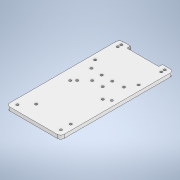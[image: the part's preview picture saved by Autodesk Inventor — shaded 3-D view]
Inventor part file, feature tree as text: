
AUTODESK INVENTOR PART (.ipt)
format: ipt  version: 2022.6 (Build 266554000, 554)  size: 208,384 bytes
history: native  units: mm
features: hole x5, sketch x5, projected_geometry x2, extrude x1, fillet x1, other x1
ambient origin geometry x8: Origin, YZ Plane, XZ Plane, XY Plane, X Axis, Y Axis, Z Axis, Center Point
bodies: Solid1 (feature_tree)
feature tree (15):
  extrude  "Extrusion1"  Depth=160.0mm
  fillet  "Fillet1"  Radius=5.0mm
  hole  "Brass stands"  [1 undecoded]
  hole  "Battery mount"  [1 undecoded]
  hole  "pi cam"  [1 undecoded]
  hole  "raspberry pi"  [1 undecoded]
  hole  "Hole7"  [1 undecoded]
  sketch  "Sketch1"  dims[d0=77.0mm d1=160.0mm d2=5.0mm d3=0.0mm]
  sketch  "Sketch3"  dims[d4=5.0mm]
  sketch  "Sketch5"  dims[d8=3.4mm d9=6.0mm d10=4.0mm d11=2.0mm d12=90.0deg d13=8.0mm d14=20.594885mm d15=147.0mm]
  sketch  "Sketch7"  dims[d18=8.0mm d31=30.0mm]
  sketch  "Sketch8"  dims[d32=46.0mm d33=55.0mm d34=3.4mm d35=6.0mm d36=4.0mm d37=2.0mm d38=90.0deg d39=8.0mm d40=20.594885mm d56=61.5mm d64=45.0mm d65=5.0mm d66=13.5mm d67=15.0mm d71=51.0mm d72=3.4mm d73=6.0mm d74=4.0mm d75=2.0mm d76=90.0deg d77=8.0mm d78=20.594885mm d79=49.0mm d80=58.0mm d81=22.0mm d82=7.75mm d83=3.4mm d84=6.0mm d85=4.0mm d86=2.0mm d87=90.0deg d88=8.0mm d89=20.594885mm d90=32.0mm d91=3.4mm d92=6.0mm d93=4.0mm d94=2.0mm d95=90.0deg d96=8.0mm d97=20.594885mm d98=10.0mm d16=20.594885mm d17=0.0625mm d19=0.375mm]
  projected_geometry  "Projected Loop1"
  other  "buck convertor"
  projected_geometry  "Projected Loop2"
note: 5 required parameter values undecoded (feature->parameter linkage not recoverable at this tier; creation-order binding heuristic only, values carry confidence <= 0.55)
